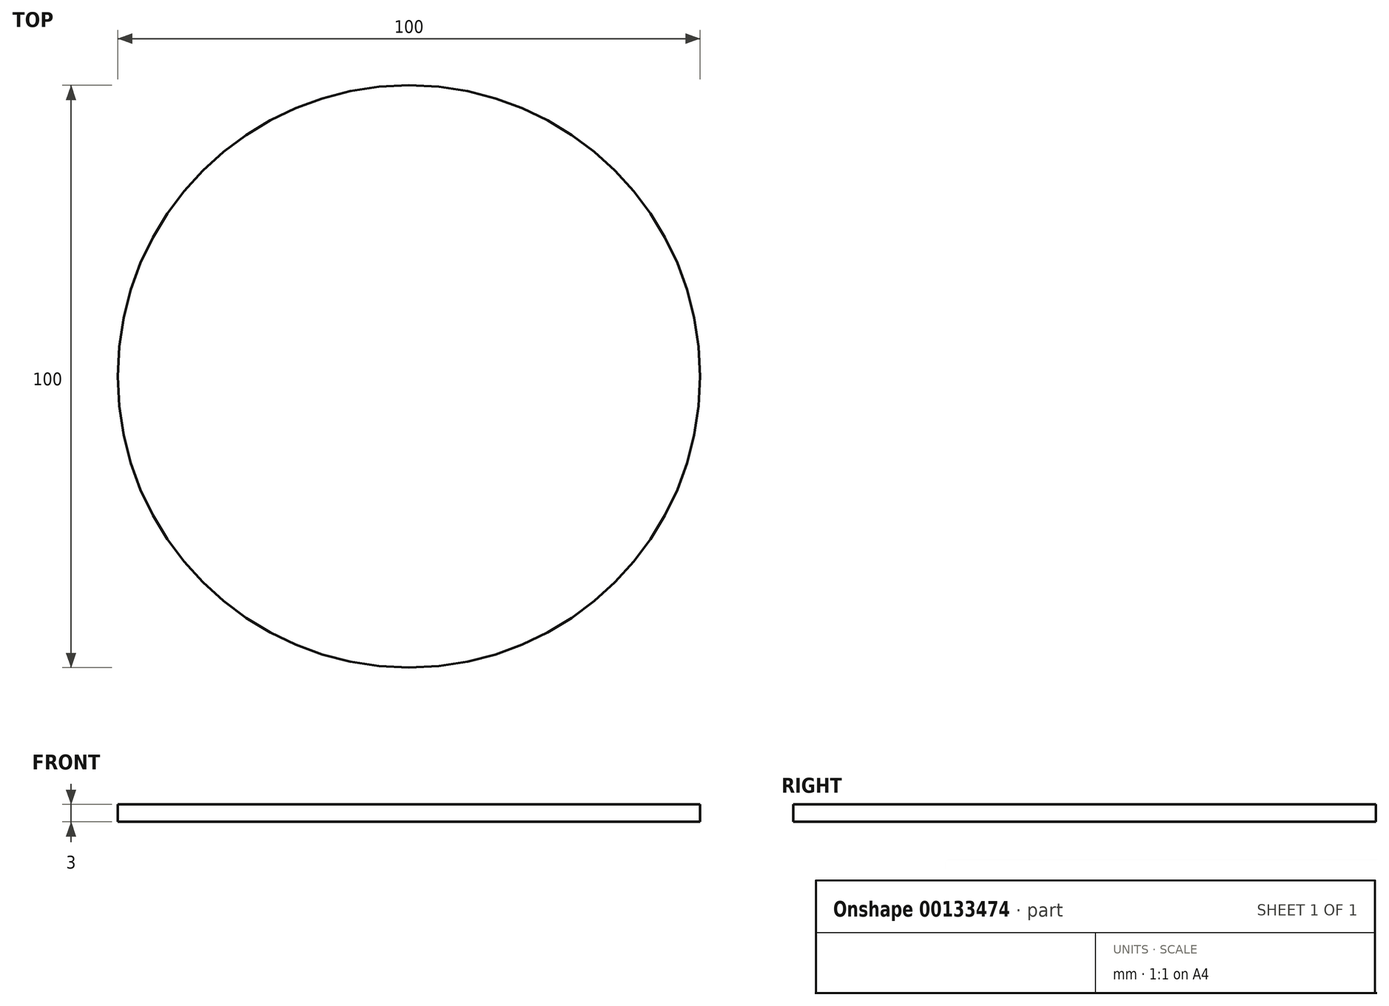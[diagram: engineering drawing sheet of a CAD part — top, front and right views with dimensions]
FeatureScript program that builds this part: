
annotation { "Feature Type Name" : "Feature", "Feature Type Description" : "" }
export const myFeature = defineFeature(function(context is Context, id is Id, definition is map)
    precondition{}
    {
        {
            var Q0;
            Q0=qCreatedBy(makeId("Top.planeOp"),FACE);
            var sketch = newSketch(context, id + "F0", { "sketchPlane" : qUnion([Q0])});
            skCircle(sketch, "E0", {"center": v(0, 0) * mm, "radius": 50 * mm});
            skSolve(sketch);
        }
        {
            var Q0;
            Q0=makeQuery(id+"F0.imprint","IMPRINT",FACE,{"disambiguationData":[TD([[makeQuery(id+"F0.imprint","IMPRINT",EDGE,{"derivedFrom":sQuery(id+"F0.wireOp",EDGE,"E0")}),1.0]])]});
            extrude(context, id + "F1", {"entities" : qUnion([Q0]), "depth" : 3 * mm});
        }
    });
